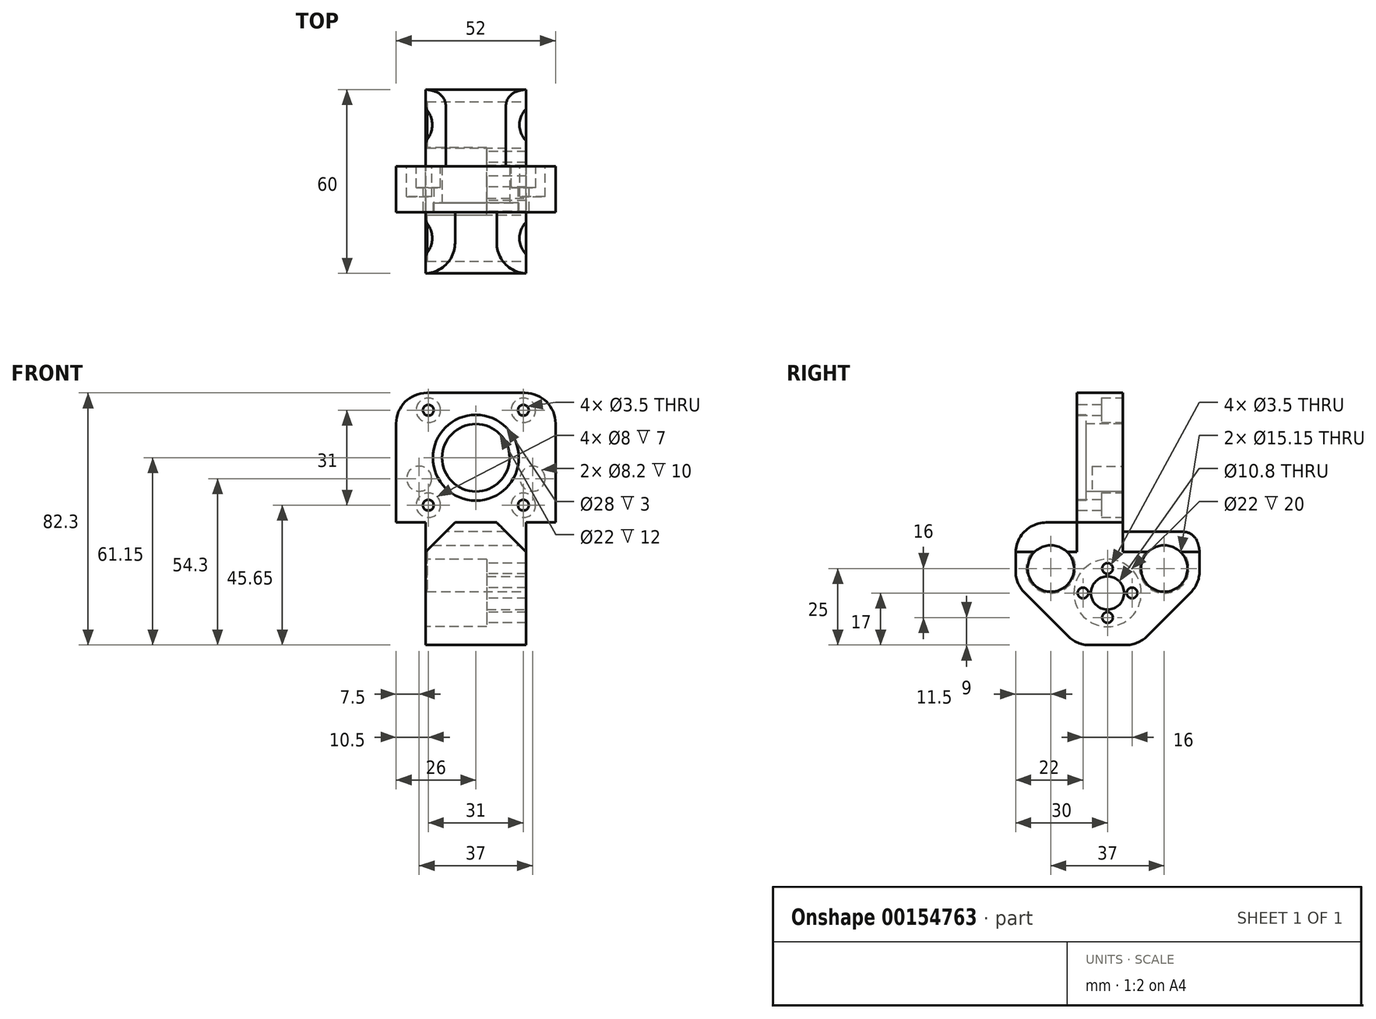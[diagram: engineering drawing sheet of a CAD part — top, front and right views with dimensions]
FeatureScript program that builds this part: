
annotation { "Feature Type Name" : "Feature", "Feature Type Description" : "" }
export const myFeature = defineFeature(function(context is Context, id is Id, definition is map)
    precondition{}
    {
        {
            var Q0;
            Q0=qCreatedBy(makeId("Top.planeOp"),FACE);
            var sketch = newSketch(context, id + "F0", { "sketchPlane" : qUnion([Q0])});
            skLineSegment(sketch, "E0.bottom", {"start": v(16.4, -30) * mm, "end": v(-16.4, -30) * mm});
            skLineSegment(sketch, "E0.top", {"start": v(16.4, 30) * mm, "end": v(-16.4, 30) * mm});
            skLineSegment(sketch, "E0.left", {"start": v(16.4, -30) * mm, "end": v(16.4, 30) * mm});
            skLineSegment(sketch, "E0.right", {"start": v(-16.4, -30) * mm, "end": v(-16.4, 30) * mm});
            skPoint(sketch, "E0.middle", {"position": v(0, 0) * mm});
            skSolve(sketch);
        }
        {
            var Q0;
            Q0=makeQuery(id+"F0.imprint","IMPRINT",FACE,{"disambiguationData":[TD([[makeQuery(id+"F0.imprint","IMPRINT",EDGE,{"derivedFrom":sQuery(id+"F0.wireOp",EDGE,"E0.bottom")}),-1.0]])]});
            extrude(context, id + "F1", {"entities" : qUnion([Q0]), "depth" : 40 * mm});
        }
        {
            var Q0;
            Q0=makeQuery(id+"F1.opExtrude","SWEPT_FACE",FACE,{"disambiguationData":[OSD([sQuery(id+"F0.wireOp",EDGE,"E0.left")])]});
            var sketch = newSketch(context, id + "F2", { "sketchPlane" : qUnion([Q0])});
            skCircle(sketch, "E1", {"center": v(-18.5, 25) * mm, "radius": 7.58 * mm});
            skCircle(sketch, "E2", {"center": v(18.5, 25) * mm, "radius": 7.58 * mm});
            skLineSegment(sketch, "E3", {"start": v(0, 40) * mm, "end": v(0, 0) * mm});
            skCircle(sketch, "E4", {"center": v(0, 17) * mm, "radius": 5.4 * mm});
            skSolve(sketch);
        }
        {
            var Q0;
            Q0 = qSketchRegion(id + "F2", true);
            extrude(context, id + "F3", {"entities" : qUnion([Q0]), "operationType" : NewBodyOperationType.REMOVE, "endBound" : BoundingType.THROUGH_ALL, "oppositeDirection" : true, "depth" : 25 * mm});
        }
        {
            var Q0;
            Q0=makeQuery(id+"F1.opExtrude","SWEPT_FACE",FACE,{"disambiguationData":[OSD([sQuery(id+"F0.wireOp",EDGE,"E0.right")])]});
            var sketch = newSketch(context, id + "F4", { "sketchPlane" : qUnion([Q0])});
            skCircle(sketch, "E5", {"center": v(0, 17) * mm, "radius": 11 * mm});
            skSolve(sketch);
        }
        {
            var Q0;
            Q0=makeQuery(id+"F4.imprint","IMPRINT",FACE,{"disambiguationData":[TD([[makeQuery(id+"F4.imprint","IMPRINT",EDGE,{"derivedFrom":sQuery(id+"F4.wireOp",EDGE,"E5")}),1.0]])]});
            extrude(context, id + "F5", {"entities" : qUnion([Q0]), "operationType" : NewBodyOperationType.REMOVE, "oppositeDirection" : true, "depth" : 20 * mm});
        }
        {
            var Q0;
            Q0=makeQuery(id+"F5.boolean.opBoolean","COPY",FACE,{"derivedFrom":makeQuery(id+"F5.opExtrude","CAP_FACE",FACE,{"disambiguationData":[OSD([sQuery(id+"F0.wireOp",EDGE,"E0.right"),sQuery(id+"F2.wireOp",EDGE,"E4"),sQuery(id+"F4.wireOp",EDGE,"E5")])],"isStart":false})});
            var sketch = newSketch(context, id + "F6", { "sketchPlane" : qUnion([Q0])});
            skCircle(sketch, "E6", {"center": v(0, 17) * mm, "radius": 8 * mm});
            skPoint(sketch, "E7", {"position": v(0, 25) * mm});
            skPoint(sketch, "E8", {"position": v(8, 17) * mm});
            skPoint(sketch, "E9", {"position": v(0, 9) * mm});
            skPoint(sketch, "E10", {"position": v(-8, 17) * mm});
            skCircle(sketch, "E11", {"center": v(0, 25) * mm, "radius": 1.75 * mm});
            skCircle(sketch, "E12", {"center": v(8, 17) * mm, "radius": 1.75 * mm});
            skCircle(sketch, "E13", {"center": v(0, 9) * mm, "radius": 1.75 * mm});
            skCircle(sketch, "E14", {"center": v(-8, 17) * mm, "radius": 1.75 * mm});
            skSolve(sketch);
        }
        {
            var Q0;
            {var subQ0=sQuery(id+"F6.wireOp",EDGE,"E11");var subQ1=sQuery(id+"F6.wireOp",EDGE,"E6");var subQ2=makeQuery(id+"F6.imprint","INTERSECT",VERTEX,{"disambiguationData":[OD(0.0)],"derivedFrom":[subQ1,subQ0]});Q0=makeQuery(id+"F6.imprint","IMPRINT",FACE,{"disambiguationData":[TD([[makeQuery(id+"F6.imprint","IMPRINT",EDGE,{"disambiguationData":[TD([[subQ2,-1.0]])],"derivedFrom":subQ1}),1.0]])]});}
            var Q1;
            {var subQ0=sQuery(id+"F6.wireOp",EDGE,"E11");var subQ1=sQuery(id+"F6.wireOp",EDGE,"E6");var subQ2=makeQuery(id+"F6.imprint","INTERSECT",VERTEX,{"disambiguationData":[OD(0.0)],"derivedFrom":[subQ1,subQ0]});Q1=makeQuery(id+"F6.imprint","IMPRINT",FACE,{"disambiguationData":[TD([[makeQuery(id+"F6.imprint","IMPRINT",EDGE,{"disambiguationData":[TD([[subQ2,-1.0]])],"derivedFrom":subQ1}),-1.0]])]});}
            var Q2;
            {var subQ0=sQuery(id+"F6.wireOp",EDGE,"E14");var subQ1=sQuery(id+"F6.wireOp",EDGE,"E6");var subQ2=makeQuery(id+"F6.imprint","INTERSECT",VERTEX,{"disambiguationData":[OD(0.0)],"derivedFrom":[subQ1,subQ0]});Q2=makeQuery(id+"F6.imprint","IMPRINT",FACE,{"disambiguationData":[TD([[makeQuery(id+"F6.imprint","IMPRINT",EDGE,{"disambiguationData":[TD([[subQ2,-1.0]])],"derivedFrom":subQ1}),-1.0]])]});}
            var Q3;
            {var subQ0=sQuery(id+"F6.wireOp",EDGE,"E14");var subQ1=sQuery(id+"F6.wireOp",EDGE,"E6");var subQ2=makeQuery(id+"F6.imprint","INTERSECT",VERTEX,{"disambiguationData":[OD(0.0)],"derivedFrom":[subQ1,subQ0]});Q3=makeQuery(id+"F6.imprint","IMPRINT",FACE,{"disambiguationData":[TD([[makeQuery(id+"F6.imprint","IMPRINT",EDGE,{"disambiguationData":[TD([[subQ2,-1.0]])],"derivedFrom":subQ1}),1.0]])]});}
            var Q4;
            {var subQ0=sQuery(id+"F6.wireOp",EDGE,"E13");var subQ1=sQuery(id+"F6.wireOp",EDGE,"E6");var subQ2=makeQuery(id+"F6.imprint","INTERSECT",VERTEX,{"disambiguationData":[OD(0.0)],"derivedFrom":[subQ1,subQ0]});Q4=makeQuery(id+"F6.imprint","IMPRINT",FACE,{"disambiguationData":[TD([[makeQuery(id+"F6.imprint","IMPRINT",EDGE,{"disambiguationData":[TD([[subQ2,-1.0]])],"derivedFrom":subQ1}),1.0]])]});}
            var Q5;
            {var subQ0=sQuery(id+"F6.wireOp",EDGE,"E13");var subQ1=sQuery(id+"F6.wireOp",EDGE,"E6");var subQ2=makeQuery(id+"F6.imprint","INTERSECT",VERTEX,{"disambiguationData":[OD(0.0)],"derivedFrom":[subQ1,subQ0]});Q5=makeQuery(id+"F6.imprint","IMPRINT",FACE,{"disambiguationData":[TD([[makeQuery(id+"F6.imprint","IMPRINT",EDGE,{"disambiguationData":[TD([[subQ2,-1.0]])],"derivedFrom":subQ1}),-1.0]])]});}
            var Q6;
            {var subQ0=sQuery(id+"F6.wireOp",EDGE,"E12");var subQ1=sQuery(id+"F6.wireOp",EDGE,"E6");var subQ2=makeQuery(id+"F6.imprint","INTERSECT",VERTEX,{"disambiguationData":[OD(0.0)],"derivedFrom":[subQ1,subQ0]});Q6=makeQuery(id+"F6.imprint","IMPRINT",FACE,{"disambiguationData":[TD([[makeQuery(id+"F6.imprint","IMPRINT",EDGE,{"disambiguationData":[TD([[subQ2,1.0]])],"derivedFrom":subQ1}),1.0]])]});}
            var Q7;
            {var subQ0=sQuery(id+"F6.wireOp",EDGE,"E12");var subQ1=sQuery(id+"F6.wireOp",EDGE,"E6");var subQ2=makeQuery(id+"F6.imprint","INTERSECT",VERTEX,{"disambiguationData":[OD(0.0)],"derivedFrom":[subQ1,subQ0]});Q7=makeQuery(id+"F6.imprint","IMPRINT",FACE,{"disambiguationData":[TD([[makeQuery(id+"F6.imprint","IMPRINT",EDGE,{"disambiguationData":[TD([[subQ2,1.0]])],"derivedFrom":subQ1}),-1.0]])]});}
            extrude(context, id + "F7", {"entities" : qUnion([Q0, Q1, Q2, Q3, Q4, Q5, Q6, Q7]), "operationType" : NewBodyOperationType.REMOVE, "endBound" : BoundingType.THROUGH_ALL, "oppositeDirection" : true, "depth" : 25 * mm});
        }
        {
            var Q0;
            Q0=makeQuery(id+"F3.boolean.opBoolean","COPY",EDGE,{"derivedFrom":makeQuery(id+"F3.opExtrude","CAP_EDGE",EDGE,{"disambiguationData":[OSD([sQuery(id+"F2.wireOp",EDGE,"E4")])],"isStart":true})});
            var Q1;
            Q1=makeQuery(id+"F3.boolean.opBoolean","COPY",EDGE,{"derivedFrom":makeQuery(id+"F3.opExtrude","CAP_EDGE",EDGE,{"disambiguationData":[OSD([sQuery(id+"F2.wireOp",EDGE,"E1")])],"isStart":true})});
            var Q2;
            Q2=makeQuery(id+"F3.boolean.opBoolean","COPY",EDGE,{"derivedFrom":makeQuery(id+"F3.opExtrude","CAP_EDGE",EDGE,{"disambiguationData":[OSD([sQuery(id+"F2.wireOp",EDGE,"E2")])],"isStart":true})});
            var Q3;
            Q3=makeQuery(id+"F3.boolean.opBoolean","INTERSECT",EDGE,{"derivedFrom":[makeQuery(id+"F1.opExtrude","SWEPT_FACE",FACE,{"disambiguationData":[OSD([sQuery(id+"F0.wireOp",EDGE,"E0.right")])]}),makeQuery(id+"F3.opExtrude","SWEPT_FACE",FACE,{"disambiguationData":[OSD([sQuery(id+"F2.wireOp",EDGE,"E2")])]})]});
            var Q4;
            Q4=makeQuery(id+"F3.boolean.opBoolean","INTERSECT",EDGE,{"derivedFrom":[makeQuery(id+"F1.opExtrude","SWEPT_FACE",FACE,{"disambiguationData":[OSD([sQuery(id+"F0.wireOp",EDGE,"E0.right")])]}),makeQuery(id+"F3.opExtrude","SWEPT_FACE",FACE,{"disambiguationData":[OSD([sQuery(id+"F2.wireOp",EDGE,"E1")])]})]});
            var Q5;
            Q5=makeQuery(id+"F5.boolean.opBoolean","COPY",EDGE,{"derivedFrom":makeQuery(id+"F5.opExtrude","CAP_EDGE",EDGE,{"disambiguationData":[OSD([sQuery(id+"F4.wireOp",EDGE,"E5")])],"isStart":true})});
            var Q6;
            Q6=makeQuery(id+"F5.boolean.opBoolean","COPY",EDGE,{"derivedFrom":makeQuery(id+"F5.opExtrude","CAP_EDGE",EDGE,{"disambiguationData":[OSD([sQuery(id+"F0.wireOp",EDGE,"E0.right"),sQuery(id+"F2.wireOp",EDGE,"E4")])],"isStart":false})});
            chamfer(context, id + "F8", {"entities" : qUnion([Q0, Q1, Q2, Q3, Q4, Q5, Q6]), "width" : 0.5 * mm, "tangentPropagation" : true});
        }
        {
            var Q0;
            Q0=makeQuery(id+"F1.opExtrude","CAP_EDGE",EDGE,{"disambiguationData":[OSD([sQuery(id+"F0.wireOp",EDGE,"E0.top")])],"isStart":true});
            var Q1;
            Q1=makeQuery(id+"F1.opExtrude","CAP_EDGE",EDGE,{"disambiguationData":[OSD([sQuery(id+"F0.wireOp",EDGE,"E0.bottom")])],"isStart":true});
            chamfer(context, id + "F9", {"entities" : qUnion([Q0, Q1]), "width" : 20 * mm, "tangentPropagation" : true});
        }
        {
            var Q0;
            Q0=makeQuery(id+"F1.opExtrude","CAP_FACE",FACE,{"disambiguationData":[OSD([sQuery(id+"F0.wireOp",EDGE,"E0.bottom"),sQuery(id+"F0.wireOp",EDGE,"E0.top"),sQuery(id+"F0.wireOp",EDGE,"E0.left"),sQuery(id+"F0.wireOp",EDGE,"E0.right")])],"isStart":false});
            var sketch = newSketch(context, id + "F10", { "sketchPlane" : qUnion([Q0])});
            skLineSegment(sketch, "E15.bottom", {"start": v(26, -10) * mm, "end": v(-26, -10) * mm});
            skLineSegment(sketch, "E15.top", {"start": v(26, 10) * mm, "end": v(-26, 10) * mm});
            skLineSegment(sketch, "E15.left", {"start": v(26, -10) * mm, "end": v(26, 10) * mm});
            skLineSegment(sketch, "E15.right", {"start": v(-26, -10) * mm, "end": v(-26, 10) * mm});
            skPoint(sketch, "E15.middle", {"position": v(0, 0) * mm});
            skSolve(sketch);
        }
        {
            var Q0;
            Q0 = qSketchRegion(id + "F10", true);
            extrude(context, id + "F11", {"entities" : qUnion([Q0]), "operationType" : NewBodyOperationType.ADD, "depth" : 42.3 * mm});
        }
        {
            var Q0;
            {var subQ0=sQuery(id+"F10.wireOp",EDGE,"E15.top");var subQ1=sQuery(id+"F10.wireOp",EDGE,"E15.bottom");var subQ2=sQuery(id+"F0.wireOp",EDGE,"E0.right");Q0=makeQuery(id+"F11.boolean.opBoolean","SPLIT",EDGE,{"disambiguationData":[TD([makeQuery(id+"F1.opExtrude","CAP_FACE",FACE,{"disambiguationData":[OSD([sQuery(id+"F0.wireOp",EDGE,"E0.bottom"),sQuery(id+"F0.wireOp",EDGE,"E0.top"),sQuery(id+"F0.wireOp",EDGE,"E0.left"),subQ2])],"isStart":false}),makeQuery(id+"F1.opExtrude","SWEPT_FACE",FACE,{"disambiguationData":[OSD([subQ2])]}),makeQuery(id+"F11.opExtrude","SWEPT_FACE",FACE,{"disambiguationData":[OSD([subQ1])]}),makeQuery(id+"F11.opExtrude","CAP_FACE",FACE,{"disambiguationData":[OSD([subQ1,subQ0,sQuery(id+"F10.wireOp",EDGE,"E15.left"),sQuery(id+"F10.wireOp",EDGE,"E15.right")])],"isStart":true}),makeQuery(id+"F11.opExtrude","SWEPT_FACE",FACE,{"disambiguationData":[OSD([subQ0])]})])],"derivedFrom":makeQuery(id+"F1.opExtrude","CAP_EDGE",EDGE,{"disambiguationData":[OSD([subQ2])],"isStart":false})});}
            var Q1;
            {var subQ0=sQuery(id+"F10.wireOp",EDGE,"E15.top");var subQ1=sQuery(id+"F10.wireOp",EDGE,"E15.bottom");var subQ2=sQuery(id+"F0.wireOp",EDGE,"E0.left");Q1=makeQuery(id+"F11.boolean.opBoolean","SPLIT",EDGE,{"disambiguationData":[TD([makeQuery(id+"F1.opExtrude","CAP_FACE",FACE,{"disambiguationData":[OSD([sQuery(id+"F0.wireOp",EDGE,"E0.bottom"),sQuery(id+"F0.wireOp",EDGE,"E0.top"),subQ2,sQuery(id+"F0.wireOp",EDGE,"E0.right")])],"isStart":false}),makeQuery(id+"F1.opExtrude","SWEPT_FACE",FACE,{"disambiguationData":[OSD([subQ2])]}),makeQuery(id+"F11.opExtrude","SWEPT_FACE",FACE,{"disambiguationData":[OSD([subQ1])]}),makeQuery(id+"F11.opExtrude","CAP_FACE",FACE,{"disambiguationData":[OSD([subQ1,subQ0,sQuery(id+"F10.wireOp",EDGE,"E15.left"),sQuery(id+"F10.wireOp",EDGE,"E15.right")])],"isStart":true}),makeQuery(id+"F11.opExtrude","SWEPT_FACE",FACE,{"disambiguationData":[OSD([subQ0])]})])],"derivedFrom":makeQuery(id+"F1.opExtrude","CAP_EDGE",EDGE,{"disambiguationData":[OSD([subQ2])],"isStart":false})});}
            chamfer(context, id + "F12", {"entities" : qUnion([Q0, Q1]), "width" : 9.6 * mm, "tangentPropagation" : true});
        }
        {
            var Q0;
            Q0=makeQuery(id+"F11.opExtrude","SWEPT_FACE",FACE,{"disambiguationData":[OSD([sQuery(id+"F10.wireOp",EDGE,"E15.bottom")])]});
            var sketch = newSketch(context, id + "F13", { "sketchPlane" : qUnion([Q0])});
            skLineSegment(sketch, "E16", {"start": v(-26, 82.3) * mm, "end": v(26, 40) * mm});
            skCircle(sketch, "E17", {"center": v(0, 61.15) * mm, "radius": 14 * mm});
            skSolve(sketch);
        }
        {
            var Q0;
            {var subQ0=sQuery(id+"F13.wireOp",EDGE,"E17");var subQ1=sQuery(id+"F13.wireOp",EDGE,"E16");var subQ2=makeQuery(id+"F13.imprint","INTERSECT",VERTEX,{"disambiguationData":[OD(0.0)],"derivedFrom":[subQ1,subQ0]});Q0=makeQuery(id+"F13.imprint","IMPRINT",FACE,{"disambiguationData":[TD([[makeQuery(id+"F13.imprint","IMPRINT",EDGE,{"disambiguationData":[TD([[subQ2,-1.0]])],"derivedFrom":subQ1}),1.0]])]});}
            var Q1;
            {var subQ0=sQuery(id+"F13.wireOp",EDGE,"E17");var subQ1=sQuery(id+"F13.wireOp",EDGE,"E16");var subQ2=makeQuery(id+"F13.imprint","INTERSECT",VERTEX,{"disambiguationData":[OD(0.0)],"derivedFrom":[subQ1,subQ0]});Q1=makeQuery(id+"F13.imprint","IMPRINT",FACE,{"disambiguationData":[TD([[makeQuery(id+"F13.imprint","IMPRINT",EDGE,{"disambiguationData":[TD([[subQ2,-1.0]])],"derivedFrom":subQ1}),-1.0]])]});}
            extrude(context, id + "F14", {"entities" : qUnion([Q0, Q1]), "operationType" : NewBodyOperationType.REMOVE, "oppositeDirection" : true, "depth" : 3 * mm});
        }
        {
            var Q0;
            Q0=makeQuery(id+"F11.opExtrude","SWEPT_FACE",FACE,{"disambiguationData":[OSD([sQuery(id+"F10.wireOp",EDGE,"E15.bottom")])]});
            var sketch = newSketch(context, id + "F15", { "sketchPlane" : qUnion([Q0])});
            skCircle(sketch, "E18", {"center": v(0, 61.15) * mm, "radius": 11 * mm});
            skCircle(sketch, "E19", {"center": v(-15.5, 76.65) * mm, "radius": 1.75 * mm});
            skCircle(sketch, "E20.0.1.0", {"center": v(-15.5, 45.65) * mm, "radius": 1.75 * mm});
            skCircle(sketch, "E20.1.0.0", {"center": v(15.5, 76.65) * mm, "radius": 1.75 * mm});
            skCircle(sketch, "E20.1.1.0", {"center": v(15.5, 45.65) * mm, "radius": 1.75 * mm});
            skLineSegment(sketch, "E20.direction1", {"start": v(-15.5, 76.65) * mm, "end": v(15.5, 76.65) * mm, "construction": true});
            skLineSegment(sketch, "E20.direction2", {"start": v(-15.5, 76.65) * mm, "end": v(-15.5, 45.65) * mm, "construction": true});
            skSolve(sketch);
        }
        {
            var Q0;
            Q0=makeQuery(id+"F15.imprint","IMPRINT",FACE,{"disambiguationData":[TD([[makeQuery(id+"F15.imprint","IMPRINT",EDGE,{"derivedFrom":sQuery(id+"F15.wireOp",EDGE,"E19")}),1.0]])]});
            var Q1;
            Q1=makeQuery(id+"F15.imprint","IMPRINT",FACE,{"disambiguationData":[TD([[makeQuery(id+"F15.imprint","IMPRINT",EDGE,{"derivedFrom":sQuery(id+"F15.wireOp",EDGE,"E20.0.1.0")}),1.0]])]});
            var Q2;
            Q2=makeQuery(id+"F15.imprint","IMPRINT",FACE,{"disambiguationData":[TD([[makeQuery(id+"F15.imprint","IMPRINT",EDGE,{"derivedFrom":sQuery(id+"F15.wireOp",EDGE,"E20.1.1.0")}),1.0]])]});
            var Q3;
            Q3=makeQuery(id+"F15.imprint","IMPRINT",FACE,{"disambiguationData":[TD([[makeQuery(id+"F15.imprint","IMPRINT",EDGE,{"derivedFrom":sQuery(id+"F15.wireOp",EDGE,"E20.1.0.0")}),1.0]])]});
            var Q4;
            Q4=makeQuery(id+"F15.imprint","IMPRINT",FACE,{"disambiguationData":[TD([[makeQuery(id+"F15.imprint","IMPRINT",EDGE,{"derivedFrom":sQuery(id+"F15.wireOp",EDGE,"E18")}),1.0]])]});
            extrude(context, id + "F16", {"entities" : qUnion([Q0, Q1, Q2, Q3, Q4]), "operationType" : NewBodyOperationType.REMOVE, "endBound" : BoundingType.THROUGH_ALL, "oppositeDirection" : true, "depth" : 25 * mm});
        }
        {
            var Q0;
            Q0=makeQuery(id+"F11.opExtrude","SWEPT_FACE",FACE,{"disambiguationData":[OSD([sQuery(id+"F10.wireOp",EDGE,"E15.top")])]});
            var sketch = newSketch(context, id + "F17", { "sketchPlane" : qUnion([Q0])});
            skCircle(sketch, "E21", {"center": v(-15.5, 76.65) * mm, "radius": 4 * mm});
            skCircle(sketch, "E22", {"center": v(15.5, 76.65) * mm, "radius": 4 * mm});
            skCircle(sketch, "E23", {"center": v(15.5, 45.65) * mm, "radius": 4 * mm});
            skCircle(sketch, "E24", {"center": v(-15.5, 45.65) * mm, "radius": 4 * mm});
            skSolve(sketch);
        }
        {
            var Q0;
            Q0 = qSketchRegion(id + "F17", true);
            extrude(context, id + "F18", {"entities" : qUnion([Q0]), "operationType" : NewBodyOperationType.REMOVE, "oppositeDirection" : true, "depth" : 12 * mm});
        }
        {
            var Q0;
            Q0=makeQuery(id+"F11.opExtrude","SWEPT_FACE",FACE,{"disambiguationData":[OSD([sQuery(id+"F10.wireOp",EDGE,"E15.top")])]});
            var sketch = newSketch(context, id + "F19", { "sketchPlane" : qUnion([Q0])});
            skCircle(sketch, "E25", {"center": v(-18.5, 54.3) * mm, "radius": 4.1 * mm});
            skLineSegment(sketch, "E26", {"start": v(0, 82.3) * mm, "end": v(0, 40) * mm});
            skCircle(sketch, "E27.MirrorC", {"center": v(18.5, 54.3) * mm, "radius": 4.1 * mm});
            skSolve(sketch);
        }
        {
            var Q0;
            Q0 = qSketchRegion(id + "F19", true);
            extrude(context, id + "F20", {"entities" : qUnion([Q0]), "operationType" : NewBodyOperationType.REMOVE, "oppositeDirection" : true, "depth" : 15 * mm});
        }
        {
            var Q0;
            Q0=makeQuery(id+"F11.opExtrude","CAP_EDGE",EDGE,{"disambiguationData":[OSD([sQuery(id+"F10.wireOp",EDGE,"E15.left")])],"isStart":false});
            var Q1;
            {var subQ0=sQuery(id+"F10.wireOp",EDGE,"E15.left");var subQ1=sQuery(id+"F10.wireOp",EDGE,"E15.top");var subQ2=sQuery(id+"F10.wireOp",EDGE,"E15.bottom");var subQ3=sQuery(id+"F0.wireOp",EDGE,"E0.left");Q1=makeQuery(id+"F12.opChamfer","BLEND_EDGE",EDGE,{"blendedFrom":[makeQuery(id+"F11.boolean.opBoolean","SPLIT",EDGE,{"disambiguationData":[TD([makeQuery(id+"F1.opExtrude","CAP_FACE",FACE,{"disambiguationData":[OSD([sQuery(id+"F0.wireOp",EDGE,"E0.bottom"),sQuery(id+"F0.wireOp",EDGE,"E0.top"),subQ3,sQuery(id+"F0.wireOp",EDGE,"E0.right")])],"isStart":false}),makeQuery(id+"F1.opExtrude","SWEPT_FACE",FACE,{"disambiguationData":[OSD([subQ3])]}),makeQuery(id+"F11.opExtrude","SWEPT_FACE",FACE,{"disambiguationData":[OSD([subQ2])]}),makeQuery(id+"F11.opExtrude","CAP_FACE",FACE,{"disambiguationData":[OSD([subQ2,subQ1,subQ0,sQuery(id+"F10.wireOp",EDGE,"E15.right")])],"isStart":true}),makeQuery(id+"F11.opExtrude","SWEPT_FACE",FACE,{"disambiguationData":[OSD([subQ1])]})])],"derivedFrom":makeQuery(id+"F1.opExtrude","CAP_EDGE",EDGE,{"disambiguationData":[OSD([subQ3])],"isStart":false})}),makeQuery(id+"F11.opExtrude","SWEPT_FACE",FACE,{"disambiguationData":[OSD([subQ0])]})],"blendedInto":[makeQuery(id+"F11.opExtrude","SWEPT_FACE",FACE,{"disambiguationData":[OSD([subQ0])]})]});}
            var Q2;
            Q2=makeQuery(id+"F11.opExtrude","CAP_EDGE",EDGE,{"disambiguationData":[OSD([sQuery(id+"F10.wireOp",EDGE,"E15.right")])],"isStart":false});
            var Q3;
            {var subQ0=sQuery(id+"F10.wireOp",EDGE,"E15.right");var subQ1=sQuery(id+"F10.wireOp",EDGE,"E15.top");var subQ2=sQuery(id+"F10.wireOp",EDGE,"E15.bottom");var subQ3=sQuery(id+"F0.wireOp",EDGE,"E0.right");Q3=makeQuery(id+"F12.opChamfer","BLEND_EDGE",EDGE,{"blendedFrom":[makeQuery(id+"F11.boolean.opBoolean","SPLIT",EDGE,{"disambiguationData":[TD([makeQuery(id+"F1.opExtrude","CAP_FACE",FACE,{"disambiguationData":[OSD([sQuery(id+"F0.wireOp",EDGE,"E0.bottom"),sQuery(id+"F0.wireOp",EDGE,"E0.top"),sQuery(id+"F0.wireOp",EDGE,"E0.left"),subQ3])],"isStart":false}),makeQuery(id+"F1.opExtrude","SWEPT_FACE",FACE,{"disambiguationData":[OSD([subQ3])]}),makeQuery(id+"F11.opExtrude","SWEPT_FACE",FACE,{"disambiguationData":[OSD([subQ2])]}),makeQuery(id+"F11.opExtrude","CAP_FACE",FACE,{"disambiguationData":[OSD([subQ2,subQ1,sQuery(id+"F10.wireOp",EDGE,"E15.left"),subQ0])],"isStart":true}),makeQuery(id+"F11.opExtrude","SWEPT_FACE",FACE,{"disambiguationData":[OSD([subQ1])]})])],"derivedFrom":makeQuery(id+"F1.opExtrude","CAP_EDGE",EDGE,{"disambiguationData":[OSD([subQ3])],"isStart":false})}),makeQuery(id+"F11.opExtrude","SWEPT_FACE",FACE,{"disambiguationData":[OSD([subQ0])]})],"blendedInto":[makeQuery(id+"F11.opExtrude","SWEPT_FACE",FACE,{"disambiguationData":[OSD([subQ0])]})]});}
            var Q4;
            Q4=makeQuery(id+"F1.opExtrude","CAP_EDGE",EDGE,{"disambiguationData":[OSD([sQuery(id+"F0.wireOp",EDGE,"E0.top")])],"isStart":false});
            var Q5;
            Q5=makeQuery(id+"F1.opExtrude","CAP_EDGE",EDGE,{"disambiguationData":[OSD([sQuery(id+"F0.wireOp",EDGE,"E0.bottom")])],"isStart":false});
            var Q6;
            {var subQ0=sQuery(id+"F0.wireOp",EDGE,"E0.bottom");Q6=makeQuery(id+"F9.opChamfer","BLEND_EDGE",EDGE,{"blendedFrom":[makeQuery(id+"F1.opExtrude","CAP_EDGE",EDGE,{"disambiguationData":[OSD([subQ0])],"isStart":true}),makeQuery(id+"F1.opExtrude","SWEPT_FACE",FACE,{"disambiguationData":[OSD([subQ0])]})],"blendedInto":[makeQuery(id+"F1.opExtrude","SWEPT_FACE",FACE,{"disambiguationData":[OSD([subQ0])]})]});}
            var Q7;
            {var subQ0=sQuery(id+"F0.wireOp",EDGE,"E0.top");Q7=makeQuery(id+"F9.opChamfer","BLEND_EDGE",EDGE,{"blendedFrom":[makeQuery(id+"F1.opExtrude","CAP_EDGE",EDGE,{"disambiguationData":[OSD([subQ0])],"isStart":true}),makeQuery(id+"F1.opExtrude","SWEPT_FACE",FACE,{"disambiguationData":[OSD([subQ0])]})],"blendedInto":[makeQuery(id+"F1.opExtrude","SWEPT_FACE",FACE,{"disambiguationData":[OSD([subQ0])]})]});}
            var Q8;
            {var subQ0=sQuery(id+"F0.wireOp",EDGE,"E0.top");Q8=makeQuery(id+"F9.opChamfer","BLEND_EDGE",EDGE,{"blendedFrom":[makeQuery(id+"F1.opExtrude","CAP_EDGE",EDGE,{"disambiguationData":[OSD([subQ0])],"isStart":true}),makeQuery(id+"F1.opExtrude","CAP_FACE",FACE,{"disambiguationData":[OSD([sQuery(id+"F0.wireOp",EDGE,"E0.bottom"),subQ0,sQuery(id+"F0.wireOp",EDGE,"E0.left"),sQuery(id+"F0.wireOp",EDGE,"E0.right")])],"isStart":true})],"blendedInto":[makeQuery(id+"F1.opExtrude","CAP_FACE",FACE,{"disambiguationData":[OSD([sQuery(id+"F0.wireOp",EDGE,"E0.bottom"),subQ0,sQuery(id+"F0.wireOp",EDGE,"E0.left"),sQuery(id+"F0.wireOp",EDGE,"E0.right")])],"isStart":true})]});}
            var Q9;
            {var subQ0=sQuery(id+"F0.wireOp",EDGE,"E0.bottom");Q9=makeQuery(id+"F9.opChamfer","BLEND_EDGE",EDGE,{"blendedFrom":[makeQuery(id+"F1.opExtrude","CAP_EDGE",EDGE,{"disambiguationData":[OSD([subQ0])],"isStart":true}),makeQuery(id+"F1.opExtrude","CAP_FACE",FACE,{"disambiguationData":[OSD([subQ0,sQuery(id+"F0.wireOp",EDGE,"E0.top"),sQuery(id+"F0.wireOp",EDGE,"E0.left"),sQuery(id+"F0.wireOp",EDGE,"E0.right")])],"isStart":true})],"blendedInto":[makeQuery(id+"F1.opExtrude","CAP_FACE",FACE,{"disambiguationData":[OSD([subQ0,sQuery(id+"F0.wireOp",EDGE,"E0.top"),sQuery(id+"F0.wireOp",EDGE,"E0.left"),sQuery(id+"F0.wireOp",EDGE,"E0.right")])],"isStart":true})]});}
            fillet(context, id + "F21", {"entities" : qUnion([Q0, Q1, Q2, Q3, Q4, Q5, Q6, Q7, Q8, Q9]), "radius" : 10 * mm, "tangentPropagation" : true, "allowEdgeOverflow" : false});
        }
        {
            var Q0;
            Q0=makeQuery(id+"F11.opExtrude","SWEPT_FACE",FACE,{"disambiguationData":[OSD([sQuery(id+"F10.wireOp",EDGE,"E15.top")])]});
            extrude(context, id + "F22", {"entities" : qUnion([Q0]), "operationType" : NewBodyOperationType.REMOVE, "oppositeDirection" : true, "depth" : 5 * mm});
        }
        {
            var Q0;
            Q0=makeQuery(id+"F22.boolean.opBoolean","COPY",FACE,{"derivedFrom":makeQuery(id+"F22.opExtrude","CAP_FACE",FACE,{"disambiguationData":[OSD([sQuery(id+"F10.wireOp",EDGE,"E15.top")])],"isStart":false})});
            var sketch = newSketch(context, id + "F23", { "sketchPlane" : qUnion([Q0])});
            skLineSegment(sketch, "E28.bottom", {"start": v(-10, 40) * mm, "end": v(10, 40) * mm});
            skLineSegment(sketch, "E28.top", {"start": v(-10, 37) * mm, "end": v(10, 37) * mm});
            skLineSegment(sketch, "E28.left", {"start": v(-10, 40) * mm, "end": v(-10, 37) * mm});
            skLineSegment(sketch, "E28.right", {"start": v(10, 40) * mm, "end": v(10, 37) * mm});
            skSolve(sketch);
        }
        {
            var Q0;
            Q0 = qSketchRegion(id + "F23", true);
            extrude(context, id + "F24", {"entities" : qUnion([Q0]), "operationType" : NewBodyOperationType.REMOVE, "endBound" : BoundingType.THROUGH_ALL, "depth" : 25 * mm});
        }
        {
            var Q0;
            {var subQ0=sQuery(id+"F0.wireOp",EDGE,"E0.top");Q0=makeQuery(id+"F24.boolean.opBoolean","INTERSECT",EDGE,{"derivedFrom":[makeQuery(id+"F21.opFillet","BLEND_FACE",FACE,{"disambiguationData":[OSD([subQ0]),TDD([makeQuery(id+"F1.opExtrude","CAP_EDGE",EDGE,{"disambiguationData":[OSD([subQ0])],"isStart":false})])]}),makeQuery(id+"F24.opExtrude","SWEPT_FACE",FACE,{"disambiguationData":[OSD([sQuery(id+"F23.wireOp",EDGE,"E28.top")])]})]});}
            fillet(context, id + "F25", {"entities" : qUnion([Q0]), "radius" : 5 * mm, "tangentPropagation" : true, "allowEdgeOverflow" : false});
        }
    });
